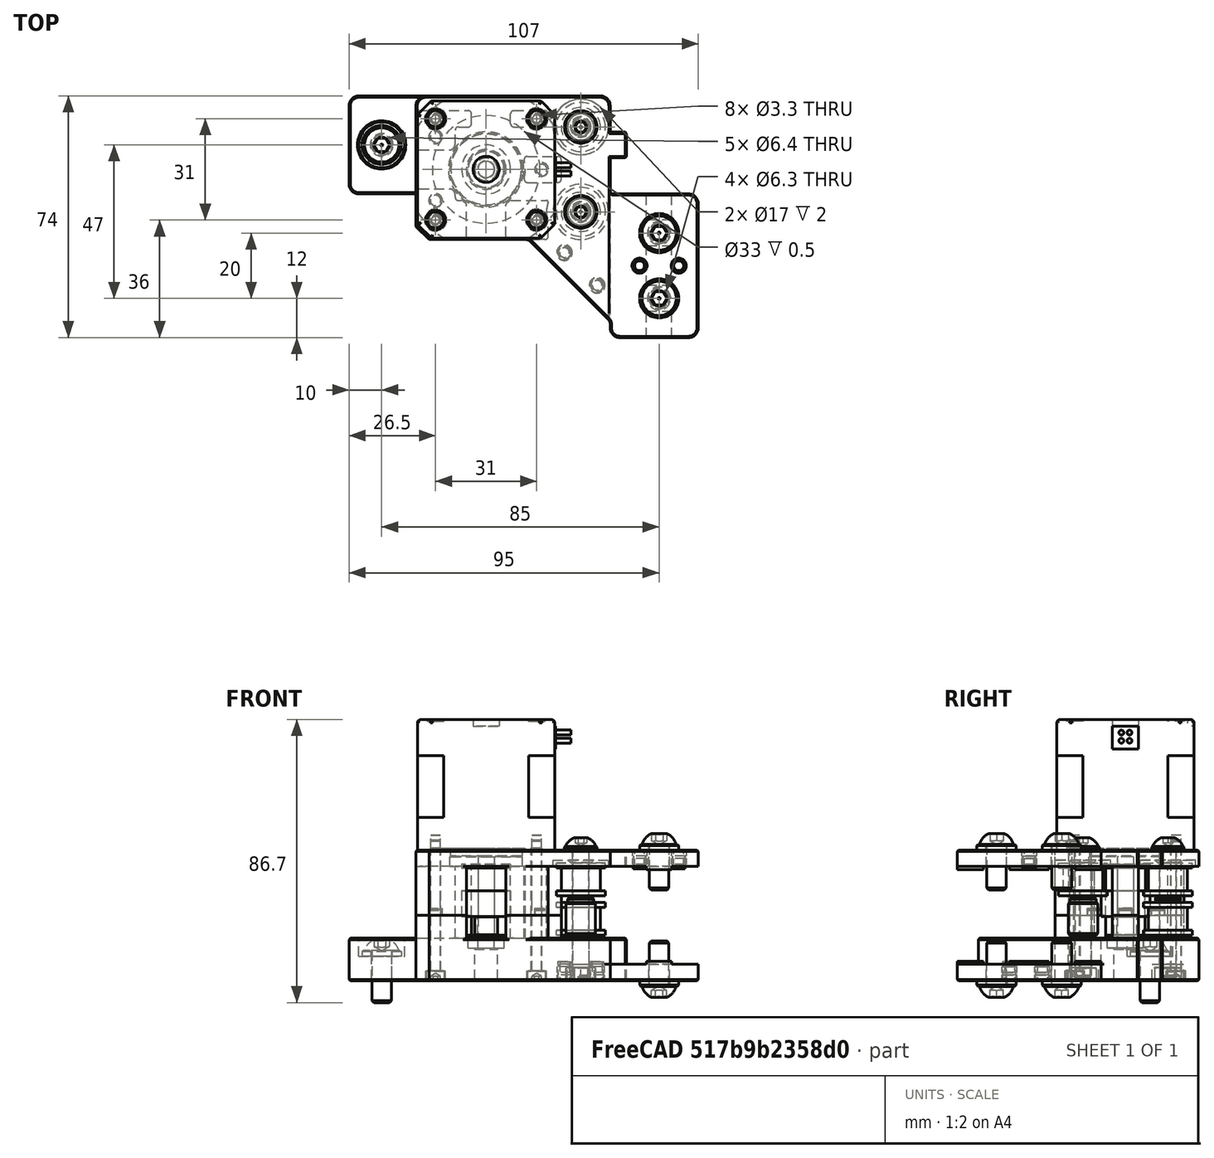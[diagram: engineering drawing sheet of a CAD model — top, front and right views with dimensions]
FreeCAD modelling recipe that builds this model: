
FCSTD DOCUMENT  (FreeCAD 0.19R24366 (Git))
Label: ab-y-motor-assembly
License: Other
LicenseURL: GPL3
objects: Part::FeaturePython×24, Part::Feature×11, Spreadsheet::Sheet×2, PartDesign::CoordinateSystem×1, App::Part×1
note: 36 computed .brp shape members not serialized (recipe doc carries the construction recipe); baked Part::Feature solids carry a one-line shape summary decoded from their .brp

FEATURE [Part::Feature] Part__Mirroring008001  label="MR115ZZ"
  shape: bbox 11 x 11 x 4 mm, 4 faces (baked)
FEATURE [Part::Feature] Part__Mirroring007001  label="20t-pulley001"
  shape: bbox 15 x 15 x 16 mm, 8 faces (baked)
FEATURE [Part::Feature] Part__Mirroring005001  label="ab-motor-idler-spacer"
  Placement = pos=(2,0,0) rot=(0,0,1;0rad)
  shape: bbox 9 x 9 x 11.85 mm, 9 faces (baked)
FEATURE [Part::Feature] Part__Mirroring003001  label="smooth-idler-6mm007"
  Placement = pos=(2,0,0) rot=(0,0,1;0rad)
  shape: bbox 15 x 15 x 10 mm, 8 faces (baked)
FEATURE [Part::Feature] Part__Mirroring002001  label="smooth-idler-6mm004"
  Placement = pos=(2,0,0) rot=(0,0,1;0rad)
  shape: bbox 15 x 15 x 10 mm, 8 faces (baked)
FEATURE [Part::Feature] Part__Mirroring001001  label="smooth-idler-6mm"
  Placement = pos=(2,0,0) rot=(0,0,1;0rad)
  shape: bbox 15 x 15 x 10 mm, 8 faces (baked)
FEATURE [Part::Feature] Part__Mirroring009002  label="motor-40mm"
  Placement = pos=(-15.5,-60.5,0) rot=(0,0,-1;1.5708rad)
  shape: bbox 47 x 42 x 67 mm, 100 faces (baked)
FEATURE [Part::Feature] Cut002001  label="motor-mount-stack-idler-spacer"
  Placement = pos=(-9,-9.5,20) rot=(0,0,1;0rad)
  shape: bbox 8 x 8 x 1.7 mm, 5 faces (baked)
FEATURE [Part::FeaturePython] Washer  label="M6-Washer"  # Fasteners workbench fastener (typed FeaturePython)
  Placement = pos=(15,-62,35) rot=(0,0,1;0rad)
  diameter = 2
  invert = true
  matchOuter = true
  offset = 0
  type = 4
FEATURE [Part::FeaturePython] Washer001  label="M6-Washer009"  # Fasteners workbench fastener (typed FeaturePython)
  Placement = pos=(15,-42,35) rot=(0,0,1;0rad)
  diameter = 2
  invert = true
  matchOuter = true
  offset = 0
  type = 4
FEATURE [Part::FeaturePython] Washer002  label="M6-Washer008"  # Fasteners workbench fastener (typed FeaturePython)
  Placement = pos=(15,-62,-5) rot=(1,0,0;3.14159rad)
  diameter = 2
  invert = false
  matchOuter = true
  offset = 0
  type = 4
FEATURE [Part::FeaturePython] Washer003  label="M6-Washer007"  # Fasteners workbench fastener (typed FeaturePython)
  Placement = pos=(15,-42,-5) rot=(1,0,0;3.14159rad)
  diameter = 2
  invert = false
  matchOuter = true
  offset = 0
  type = 4
FEATURE [Part::FeaturePython] Washer004  label="M6-Washer006"  # Fasteners workbench fastener (typed FeaturePython)
  Placement = pos=(-70,-15,2.5) rot=(0,0,1;0rad)
  diameter = 2
  invert = true
  matchOuter = true
  offset = 0
  type = 4
FEATURE [Part::FeaturePython] Screw  label="M6x16-Screw"  # Fasteners workbench fastener (typed FeaturePython)
  Placement = pos=(-70,-15,4.3) rot=(0,0,1;0rad)
  baseObject = -> Washer004 [Edge1]
  diameter = 4
  invert = false
  leftHanded = false
  length = 3
  lengthCustom = 16
  matchOuter = true
  offset = 0
  thread = false
  type = 39
FEATURE [Part::FeaturePython] Screw001  label="M6x14-Screw001"  # Fasteners workbench fastener (typed FeaturePython)
  Placement = pos=(15,-42,36.8) rot=(0,0,1;0rad)
  baseObject = -> Washer001 [Edge1]
  diameter = 4
  invert = false
  leftHanded = false
  length = 2
  lengthCustom = 14
  matchOuter = true
  offset = 0
  thread = false
  type = 39
FEATURE [Part::FeaturePython] Screw002  label="M6x14-Screw"  # Fasteners workbench fastener (typed FeaturePython)
  Placement = pos=(15,-62,36.8) rot=(0,0,1;0rad)
  baseObject = -> Washer [Edge1]
  diameter = 4
  invert = false
  leftHanded = false
  length = 2
  lengthCustom = 14
  matchOuter = true
  offset = 0
  thread = false
  type = 39
FEATURE [Part::FeaturePython] Screw003  label="M6x14-Screw003"  # Fasteners workbench fastener (typed FeaturePython)
  Placement = pos=(15,-62,-6.8) rot=(1,0,0;3.14159rad)
  baseObject = -> Washer002 [Edge1]
  diameter = 4
  invert = false
  leftHanded = false
  length = 2
  lengthCustom = 14
  matchOuter = true
  offset = 0
  thread = false
  type = 39
FEATURE [Part::FeaturePython] Screw004  label="M6x14-Screw002"  # Fasteners workbench fastener (typed FeaturePython)
  Placement = pos=(15,-42,-6.8) rot=(1,0,0;3.14159rad)
  baseObject = -> Washer003 [Edge1]
  diameter = 4
  invert = false
  leftHanded = false
  length = 2
  lengthCustom = 14
  matchOuter = true
  offset = 0
  thread = false
  type = 39
FEATURE [Part::FeaturePython] Nut  label="M5-Nut"  # Fasteners workbench fastener (typed FeaturePython)
  Placement = pos=(-9,-35.5,-1) rot=(1,0,0;3.14159rad)
  diameter = 7
  invert = false
  leftHanded = false
  matchOuter = true
  offset = 0
  thread = false
  type = 7
FEATURE [Part::FeaturePython] Nut001  label="M5-Nut001"  # Fasteners workbench fastener (typed FeaturePython)
  Placement = pos=(-9,-9.5,-1) rot=(1,0,0;3.14159rad)
  diameter = 7
  invert = false
  leftHanded = false
  matchOuter = true
  offset = 0
  thread = false
  type = 7
FEATURE [Part::FeaturePython] Screw007  label="M3x40-Screw"  # Fasteners workbench fastener (typed FeaturePython)
  Placement = pos=(-22.5,-38,-2) rot=(1,0,0;3.14159rad)
  diameter = 4
  invert = false
  leftHanded = false
  length = 10
  lengthCustom = 40
  matchOuter = true
  offset = 0
  thread = false
  type = 33
FEATURE [Part::FeaturePython] Screw008  label="M3x40-Screw005"  # Fasteners workbench fastener (typed FeaturePython)
  Placement = pos=(-53.5,-38,-2) rot=(1,0,0;3.14159rad)
  diameter = 4
  invert = false
  leftHanded = false
  length = 10
  lengthCustom = 40
  matchOuter = true
  offset = 0
  thread = false
  type = 33
FEATURE [Part::FeaturePython] Screw009  label="M3x40-Screw004"  # Fasteners workbench fastener (typed FeaturePython)
  Placement = pos=(-53.5,-7,-2) rot=(1,0,0;3.14159rad)
  diameter = 4
  invert = false
  leftHanded = false
  length = 10
  lengthCustom = 40
  matchOuter = true
  offset = 0
  thread = false
  type = 33
FEATURE [Part::FeaturePython] Screw010  label="M3x40-Screw003"  # Fasteners workbench fastener (typed FeaturePython)
  Placement = pos=(-22.5,-7,-2) rot=(1,0,0;3.14159rad)
  diameter = 4
  invert = false
  leftHanded = false
  length = 10
  lengthCustom = 40
  matchOuter = true
  offset = 0
  thread = false
  type = 33
FEATURE [Part::FeaturePython] HeatSet  label="M3x4-HeatSet"  # WARN: FeaturePython — macro-defined, semantics opaque (R4)
  Placement = pos=(21,-52,35) rot=(0,0,1;0rad)
  diameter = 2
  invert = true
  offset = 0
FEATURE [Part::FeaturePython] HeatSet001  label="M3x4-HeatSet001"  # WARN: FeaturePython — macro-defined, semantics opaque (R4)
  Placement = pos=(9,-52,35) rot=(0,0,1;0rad)
  diameter = 2
  invert = true
  offset = 0
FEATURE [Part::FeaturePython] HeatSet002  label="M3x4-HeatSet002"  # WARN: FeaturePython — macro-defined, semantics opaque (R4)
  Placement = pos=(-4,-58,-5) rot=(1,0,0;3.14159rad)
  diameter = 2
  invert = false
  offset = 0
FEATURE [Part::FeaturePython] HeatSet003  label="M3x4-HeatSet003"  # WARN: FeaturePython — macro-defined, semantics opaque (R4)
  Placement = pos=(-14,-48,-5) rot=(1,0,0;3.14159rad)
  diameter = 2
  invert = false
  offset = 0
FEATURE [Part::Feature] Part__Mirroring009001  label="ab-motor-right-pulley-spacer"
  shape: bbox 6.9 x 6.9 x 5.5 mm, 4 faces (baked)
FEATURE [PartDesign::CoordinateSystem] LCS_ab_y_motor  label="LCS_ab-y-motor"
  AttacherType = Attacher::AttachEngine3D
FEATURE [Part::FeaturePython] Washer005  label="M5-Washer"  # Fasteners workbench fastener (typed FeaturePython)
  Placement = pos=(-9,-35.5,35) rot=(0,0,1;0rad)
  diameter = 1
  invert = true
  matchOuter = true
  offset = 0
  type = 4
FEATURE [Part::FeaturePython] Washer006  label="M5-Washer001"  # Fasteners workbench fastener (typed FeaturePython)
  Placement = pos=(-9,-9.5,35) rot=(0,0,1;0rad)
  diameter = 1
  invert = true
  matchOuter = true
  offset = 0
  type = 4
FEATURE [Part::FeaturePython] Screw011  label="M5x40-Screw"  # Fasteners workbench fastener (typed FeaturePython)
  Placement = pos=(-9,-35.5,36.1) rot=(0,0,1;0rad)
  baseObject = -> Washer005 [Edge1]
  diameter = 3
  invert = false
  leftHanded = false
  length = 9
  lengthCustom = 40
  matchOuter = true
  offset = 0
  thread = false
  type = 40
FEATURE [Part::FeaturePython] Screw012  label="M5x40-Screw001"  # Fasteners workbench fastener (typed FeaturePython)
  Placement = pos=(-9,-9.5,36.1) rot=(0,0,1;0rad)
  baseObject = -> Washer006 [Edge1]
  diameter = 3
  invert = false
  leftHanded = false
  length = 9
  lengthCustom = 40
  matchOuter = true
  offset = 0
  thread = false
  type = 40
FEATURE [Spreadsheet::Sheet] Fasteners_BOM
  cells = A1=Type; B1=Qty; A2=Heat Set Insert M3; B2=8; A3=ISO4032 Nut M5; B3=4; A4=ISO4762 Screw M3x40; B4=8; A5=ISO7090 Washer M5; B5=8; A6=ISO7090 Washer M6; B6=20; A7=ISO7380-1 Screw M5x40; B7=4; A8=ISO7380-1 Screw M6x14; B8=8; A9=ISO7380-1 Screw M6x16; B9=2
FEATURE [Spreadsheet::Sheet] Fasteners_BOM001
  cells = A1=Type; B1=Qty; A2=Heat Set Insert M3; B2=8; A3=ISO4032 Nut M5; B3=4; A4=ISO4762 Screw M3x40; B4=8; A5=ISO7090 Washer M5; B5=8; A6=ISO7090 Washer M6; B6=20; A7=ISO7380-1 Screw M5x40; B7=4; A8=ISO7380-1 Screw M6x14; B8=8; A9=ISO7380-1 Screw M6x16; B9=2
FEATURE [Part::Feature] Part__Mirroring009003004002  label="ab-motor-top-right"
  Placement = pos=(0,-30,0) rot=(0,0,1;0rad)
  shape: bbox 86.5 x 74 x 20 mm, 159 faces (baked)
FEATURE [Part::Feature] Part__Mirroring001002  label="ab-motor-bottom-right"
  Placement = pos=(0,-30,0) rot=(0,0,1;0rad)
  shape: bbox 107 x 74 x 22 mm, 227 faces (baked)
FEATURE [App::Part] Part  label="ab-y-motor"
  Group = -> [Part__Mirroring009001,Part__Mirroring008001,Part__Mirroring007001,Part__Mirroring005001,Part__Mirroring003001,Part__Mirroring002001,Part__Mirroring001001,Part__Mirroring009002,Cut002001,Screw002,Screw001,Washer001,Washer,Screw,Screw004,Nut001,Screw010,Screw007,Screw003,Washer003,Screw009,Washer004,Screw008,Nut,Washer002,HeatSet,HeatSet001,HeatSet002,HeatSet003,LCS_ab_y_motor,Washer005,Washer006,+4 more]
  Origin = -> Origin
